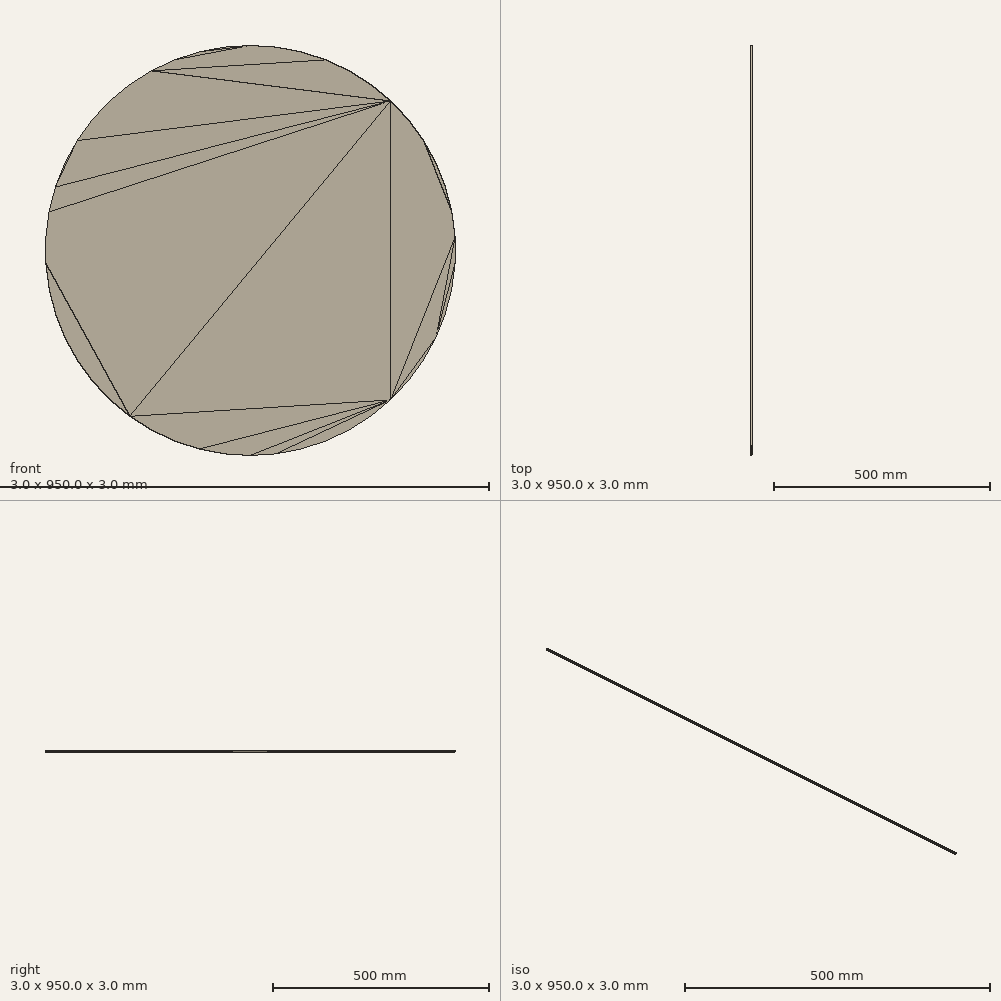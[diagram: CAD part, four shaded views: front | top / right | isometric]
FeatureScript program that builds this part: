
annotation { "Feature Type Name" : "Feature", "Feature Type Description" : "" }
export const myFeature = defineFeature(function(context is Context, id is Id, definition is map)
    precondition{}
    {
        {
            var Q0;
            Q0=qCreatedBy(makeId("Front.planeOp"),FACE);
            var sketch = newSketch(context, id + "F0", { "sketchPlane" : qUnion([Q0])});
            skCircle(sketch, "E0", {"center": v(-4.29, 40.3) * mm, "radius": 1.5 * mm});
            skSolve(sketch);
        }
        {
            var Q0;
            Q0=qSketchRegion(id+"F0",true);
            extrude(context, id + "F1", {"entities" : qUnion([Q0]), "depth" : 950 * mm, "offsetDistance" : 25 * mm});
        }
    });
